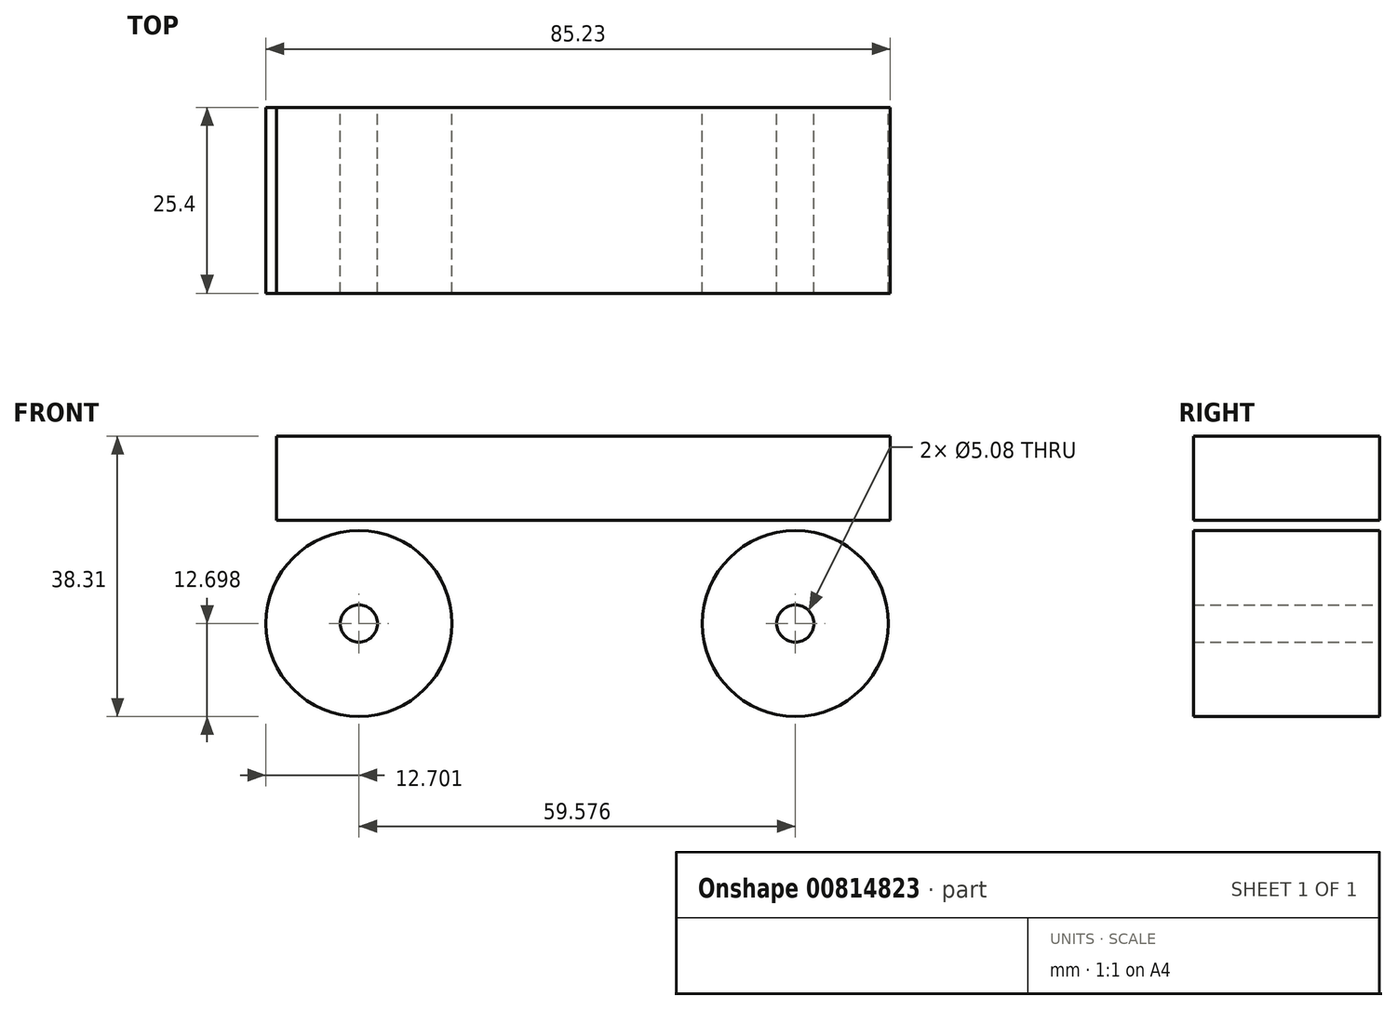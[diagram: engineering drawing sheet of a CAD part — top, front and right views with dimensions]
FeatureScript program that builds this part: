
annotation { "Feature Type Name" : "Feature", "Feature Type Description" : "" }
export const myFeature = defineFeature(function(context is Context, id is Id, definition is map)
    precondition{}
    {
        {
            var Q0;
            Q0=qCreatedBy(makeId("Front.planeOp"),FACE);
            var sketch = newSketch(context, id + "F0", { "sketchPlane" : qUnion([Q0])});
            skLineSegment(sketch, "E0.bottom", {"start": v(-42.16, 22.6) * mm, "end": v(41.59, 22.6) * mm});
            skLineSegment(sketch, "E0.top", {"start": v(-42.16, 11.08) * mm, "end": v(41.59, 11.08) * mm});
            skLineSegment(sketch, "E0.left", {"start": v(-42.16, 22.6) * mm, "end": v(-42.16, 11.08) * mm});
            skLineSegment(sketch, "E0.right", {"start": v(41.59, 22.6) * mm, "end": v(41.59, 11.08) * mm});
            skCircle(sketch, "E1", {"center": v(-30.94, -3.02) * mm, "radius": 12.7 * mm});
            skCircle(sketch, "E2", {"center": v(28.64, -3.02) * mm, "radius": 12.7 * mm});
            skCircle(sketch, "E3", {"center": v(-30.94, -3.02) * mm, "radius": 2.54 * mm});
            skCircle(sketch, "E4", {"center": v(28.64, -3.02) * mm, "radius": 2.54 * mm});
            skSolve(sketch);
        }
        {
            var Q0;
            Q0 = qSketchRegion(id + "F0", true);
            extrude(context, id + "F1", {"entities" : qUnion([Q0]), "depth" : 25.4 * mm, "offsetDistance" : 25.4 * mm});
        }
    });
